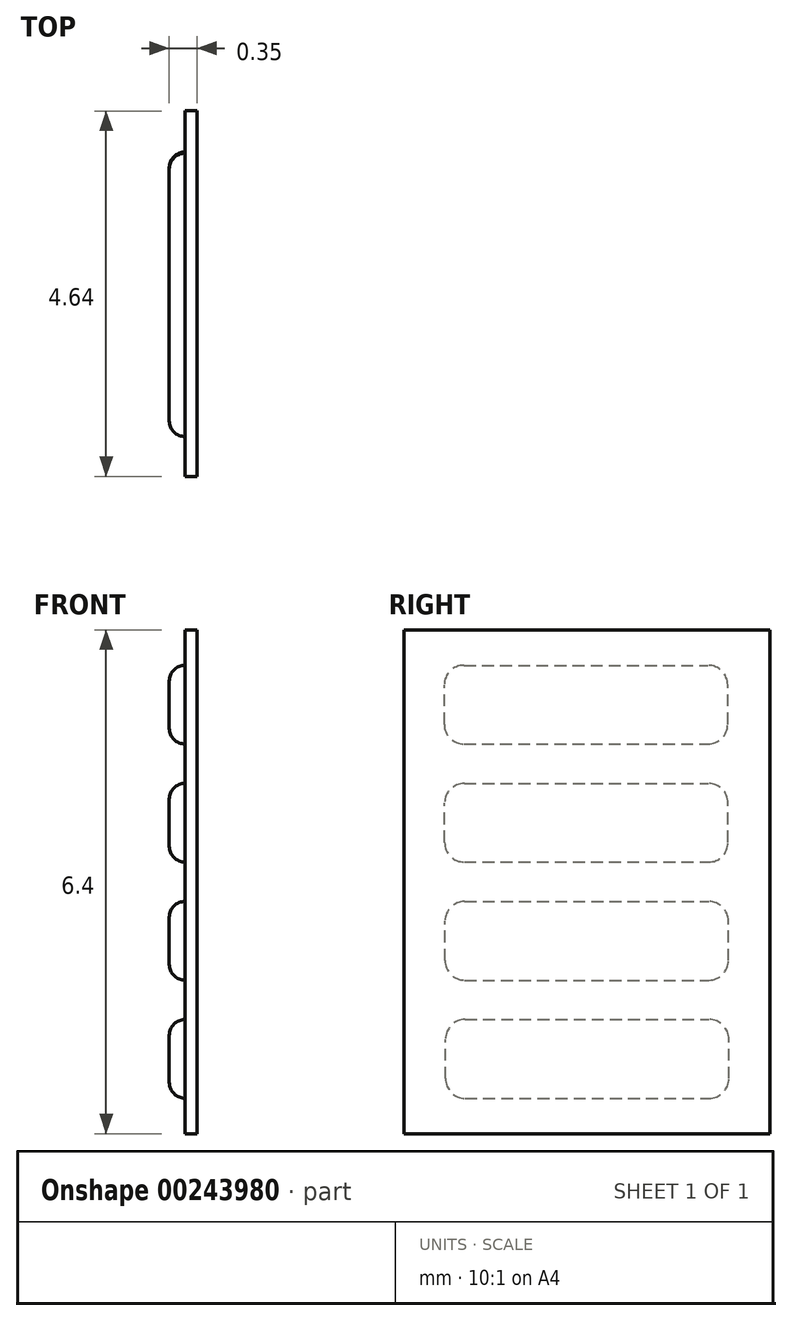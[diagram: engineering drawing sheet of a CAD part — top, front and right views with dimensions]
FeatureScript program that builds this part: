
annotation { "Feature Type Name" : "Feature", "Feature Type Description" : "" }
export const myFeature = defineFeature(function(context is Context, id is Id, definition is map)
    precondition{}
    {
        {
            var Q0;
            Q0=qCreatedBy(makeId("Right.planeOp"),FACE);
            var sketch = newSketch(context, id + "F0", { "sketchPlane" : qUnion([Q0])});
            skLineSegment(sketch, "E0.bottom", {"start": v(-2.33, 0) * mm, "end": v(2.33, 0) * mm});
            skLineSegment(sketch, "E0.top", {"start": v(-2.33, 6.4) * mm, "end": v(2.32, 6.4) * mm});
            skLineSegment(sketch, "E0.left", {"start": v(-2.33, 0) * mm, "end": v(-2.33, 6.4) * mm});
            skLineSegment(sketch, "E0.right", {"start": v(2.33, 0) * mm, "end": v(2.32, 6.4) * mm});
            skSolve(sketch);
        }
        {
            var Q0;
            Q0 = qSketchRegion(id + "F0", true);
            extrude(context, id + "F1", {"entities" : qUnion([Q0]), "oppositeDirection" : true, "depth" : 0.15 * mm});
        }
        {
            var Q0;
            Q0=makeQuery(id+"F1.opExtrude","CAP_FACE",FACE,{"disambiguationData":[OSD([sQuery(id+"F0.wireOp",EDGE,"E0.bottom"),sQuery(id+"F0.wireOp",EDGE,"E0.top"),sQuery(id+"F0.wireOp",EDGE,"E0.left"),sQuery(id+"F0.wireOp",EDGE,"E0.right")])],"isStart":false});
            var sketch = newSketch(context, id + "F2", { "sketchPlane" : qUnion([Q0])});
            skLineSegment(sketch, "E1.bottom", {"start": v(1.55, 0.45) * mm, "end": v(-1.55, 0.45) * mm});
            skLineSegment(sketch, "E1.top", {"start": v(1.55, 1.45) * mm, "end": v(-1.55, 1.45) * mm});
            skLineSegment(sketch, "E1.left", {"start": v(1.8, 0.7) * mm, "end": v(1.8, 1.2) * mm});
            skLineSegment(sketch, "E1.right", {"start": v(-1.8, 0.7) * mm, "end": v(-1.8, 1.2) * mm});
            skPoint(sketch, "E1.middle", {"position": v(0, 0.95) * mm});
            skPoint(sketch, "E2.visualSharp", {"position": v(-1.8, 0.45) * mm});
            skArc(sketch, "E2.filletArc", {"start": v(-1.8, 0.7) * mm, "mid": v(-1.73, 0.52) * mm, "end": v(-1.55, 0.45) * mm});
            skPoint(sketch, "E3.visualSharp", {"position": v(-1.8, 1.45) * mm});
            skArc(sketch, "E3.filletArc", {"start": v(-1.55, 1.45) * mm, "mid": v(-1.73, 1.38) * mm, "end": v(-1.8, 1.2) * mm});
            skPoint(sketch, "E4.visualSharp", {"position": v(1.8, 1.45) * mm});
            skArc(sketch, "E4.filletArc", {"start": v(1.8, 1.2) * mm, "mid": v(1.73, 1.38) * mm, "end": v(1.55, 1.45) * mm});
            skPoint(sketch, "E5.visualSharp", {"position": v(1.8, 0.45) * mm});
            skArc(sketch, "E5.filletArc", {"start": v(1.55, 0.45) * mm, "mid": v(1.73, 0.52) * mm, "end": v(1.8, 0.7) * mm});
            skLineSegment(sketch, "E6.1.0.0", {"start": v(1.55, 1.95) * mm, "end": v(-1.55, 1.95) * mm});
            skLineSegment(sketch, "E6.1.0.1", {"start": v(1.55, 2.95) * mm, "end": v(-1.55, 2.95) * mm});
            skArc(sketch, "E6.1.0.2", {"start": v(1.8, 2.7) * mm, "mid": v(1.73, 2.88) * mm, "end": v(1.55, 2.95) * mm});
            skLineSegment(sketch, "E6.1.0.3", {"start": v(1.8, 2.2) * mm, "end": v(1.8, 2.7) * mm});
            skArc(sketch, "E6.1.0.4", {"start": v(1.55, 1.95) * mm, "mid": v(1.73, 2.02) * mm, "end": v(1.8, 2.2) * mm});
            skArc(sketch, "E6.1.0.5", {"start": v(-1.8, 2.2) * mm, "mid": v(-1.72, 2.02) * mm, "end": v(-1.55, 1.95) * mm});
            skLineSegment(sketch, "E6.1.0.6", {"start": v(-1.8, 2.2) * mm, "end": v(-1.8, 2.7) * mm});
            skArc(sketch, "E6.1.0.7", {"start": v(-1.55, 2.95) * mm, "mid": v(-1.72, 2.88) * mm, "end": v(-1.8, 2.7) * mm});
            skLineSegment(sketch, "E6.2.0.0", {"start": v(1.56, 3.45) * mm, "end": v(-1.54, 3.45) * mm});
            skLineSegment(sketch, "E6.2.0.1", {"start": v(1.56, 4.45) * mm, "end": v(-1.54, 4.45) * mm});
            skArc(sketch, "E6.2.0.2", {"start": v(1.8, 4.2) * mm, "mid": v(1.74, 4.38) * mm, "end": v(1.56, 4.45) * mm});
            skLineSegment(sketch, "E6.2.0.3", {"start": v(1.8, 3.7) * mm, "end": v(1.8, 4.2) * mm});
            skArc(sketch, "E6.2.0.4", {"start": v(1.56, 3.45) * mm, "mid": v(1.74, 3.52) * mm, "end": v(1.8, 3.7) * mm});
            skArc(sketch, "E6.2.0.5", {"start": v(-1.8, 3.7) * mm, "mid": v(-1.72, 3.52) * mm, "end": v(-1.54, 3.45) * mm});
            skLineSegment(sketch, "E6.2.0.6", {"start": v(-1.8, 3.7) * mm, "end": v(-1.8, 4.2) * mm});
            skArc(sketch, "E6.2.0.7", {"start": v(-1.54, 4.45) * mm, "mid": v(-1.72, 4.38) * mm, "end": v(-1.8, 4.2) * mm});
            skLineSegment(sketch, "E6.3.0.0", {"start": v(1.56, 4.95) * mm, "end": v(-1.54, 4.95) * mm});
            skLineSegment(sketch, "E6.3.0.1", {"start": v(1.56, 5.95) * mm, "end": v(-1.54, 5.95) * mm});
            skArc(sketch, "E6.3.0.2", {"start": v(1.81, 5.7) * mm, "mid": v(1.74, 5.88) * mm, "end": v(1.56, 5.95) * mm});
            skLineSegment(sketch, "E6.3.0.3", {"start": v(1.81, 5.2) * mm, "end": v(1.81, 5.7) * mm});
            skArc(sketch, "E6.3.0.4", {"start": v(1.56, 4.95) * mm, "mid": v(1.74, 5.02) * mm, "end": v(1.81, 5.2) * mm});
            skArc(sketch, "E6.3.0.5", {"start": v(-1.79, 5.2) * mm, "mid": v(-1.71, 5.02) * mm, "end": v(-1.54, 4.95) * mm});
            skLineSegment(sketch, "E6.3.0.6", {"start": v(-1.79, 5.2) * mm, "end": v(-1.79, 5.7) * mm});
            skArc(sketch, "E6.3.0.7", {"start": v(-1.54, 5.95) * mm, "mid": v(-1.71, 5.88) * mm, "end": v(-1.79, 5.7) * mm});
            skLineSegment(sketch, "E6.direction1", {"start": v(-1.55, 0.45) * mm, "end": v(-1.55, 1.95) * mm, "construction": true});
            skSolve(sketch);
        }
        {
            var Q0;
            Q0 = qSketchRegion(id + "F2", true);
            extrude(context, id + "F3", {"entities" : qUnion([Q0]), "depth" : 0.2 * mm});
        }
        {
            var Q0;
            Q0=makeQuery(id+"F3.opExtrude","CAP_FACE",FACE,{"disambiguationData":[OSD([sQuery(id+"F2.wireOp",EDGE,"E6.3.0.0"),sQuery(id+"F2.wireOp",EDGE,"E6.3.0.1"),sQuery(id+"F2.wireOp",EDGE,"E6.3.0.2"),sQuery(id+"F2.wireOp",EDGE,"E6.3.0.3"),sQuery(id+"F2.wireOp",EDGE,"E6.3.0.4"),sQuery(id+"F2.wireOp",EDGE,"E6.3.0.5"),sQuery(id+"F2.wireOp",EDGE,"E6.3.0.6"),sQuery(id+"F2.wireOp",EDGE,"E6.3.0.7")])],"isStart":false});
            var Q1;
            Q1=makeQuery(id+"F3.opExtrude","CAP_FACE",FACE,{"disambiguationData":[OSD([sQuery(id+"F2.wireOp",EDGE,"E6.2.0.0"),sQuery(id+"F2.wireOp",EDGE,"E6.2.0.1"),sQuery(id+"F2.wireOp",EDGE,"E6.2.0.2"),sQuery(id+"F2.wireOp",EDGE,"E6.2.0.3"),sQuery(id+"F2.wireOp",EDGE,"E6.2.0.4"),sQuery(id+"F2.wireOp",EDGE,"E6.2.0.5"),sQuery(id+"F2.wireOp",EDGE,"E6.2.0.6"),sQuery(id+"F2.wireOp",EDGE,"E6.2.0.7")])],"isStart":false});
            var Q2;
            Q2=makeQuery(id+"F3.opExtrude","CAP_FACE",FACE,{"disambiguationData":[OSD([sQuery(id+"F2.wireOp",EDGE,"E6.1.0.0"),sQuery(id+"F2.wireOp",EDGE,"E6.1.0.1"),sQuery(id+"F2.wireOp",EDGE,"E6.1.0.2"),sQuery(id+"F2.wireOp",EDGE,"E6.1.0.3"),sQuery(id+"F2.wireOp",EDGE,"E6.1.0.4"),sQuery(id+"F2.wireOp",EDGE,"E6.1.0.5"),sQuery(id+"F2.wireOp",EDGE,"E6.1.0.6"),sQuery(id+"F2.wireOp",EDGE,"E6.1.0.7")])],"isStart":false});
            var Q3;
            Q3=makeQuery(id+"F3.opExtrude","CAP_FACE",FACE,{"disambiguationData":[OSD([sQuery(id+"F2.wireOp",EDGE,"E1.bottom"),sQuery(id+"F2.wireOp",EDGE,"E1.top"),sQuery(id+"F2.wireOp",EDGE,"E1.left"),sQuery(id+"F2.wireOp",EDGE,"E1.right"),sQuery(id+"F2.wireOp",EDGE,"E2.filletArc"),sQuery(id+"F2.wireOp",EDGE,"E3.filletArc"),sQuery(id+"F2.wireOp",EDGE,"E4.filletArc"),sQuery(id+"F2.wireOp",EDGE,"E5.filletArc")])],"isStart":false});
            fillet(context, id + "F4", {"entities" : qUnion([Q0, Q1, Q2, Q3]), "radius" : 0.2 * mm, "tangentPropagation" : true, "allowEdgeOverflow" : false});
        }
    });
